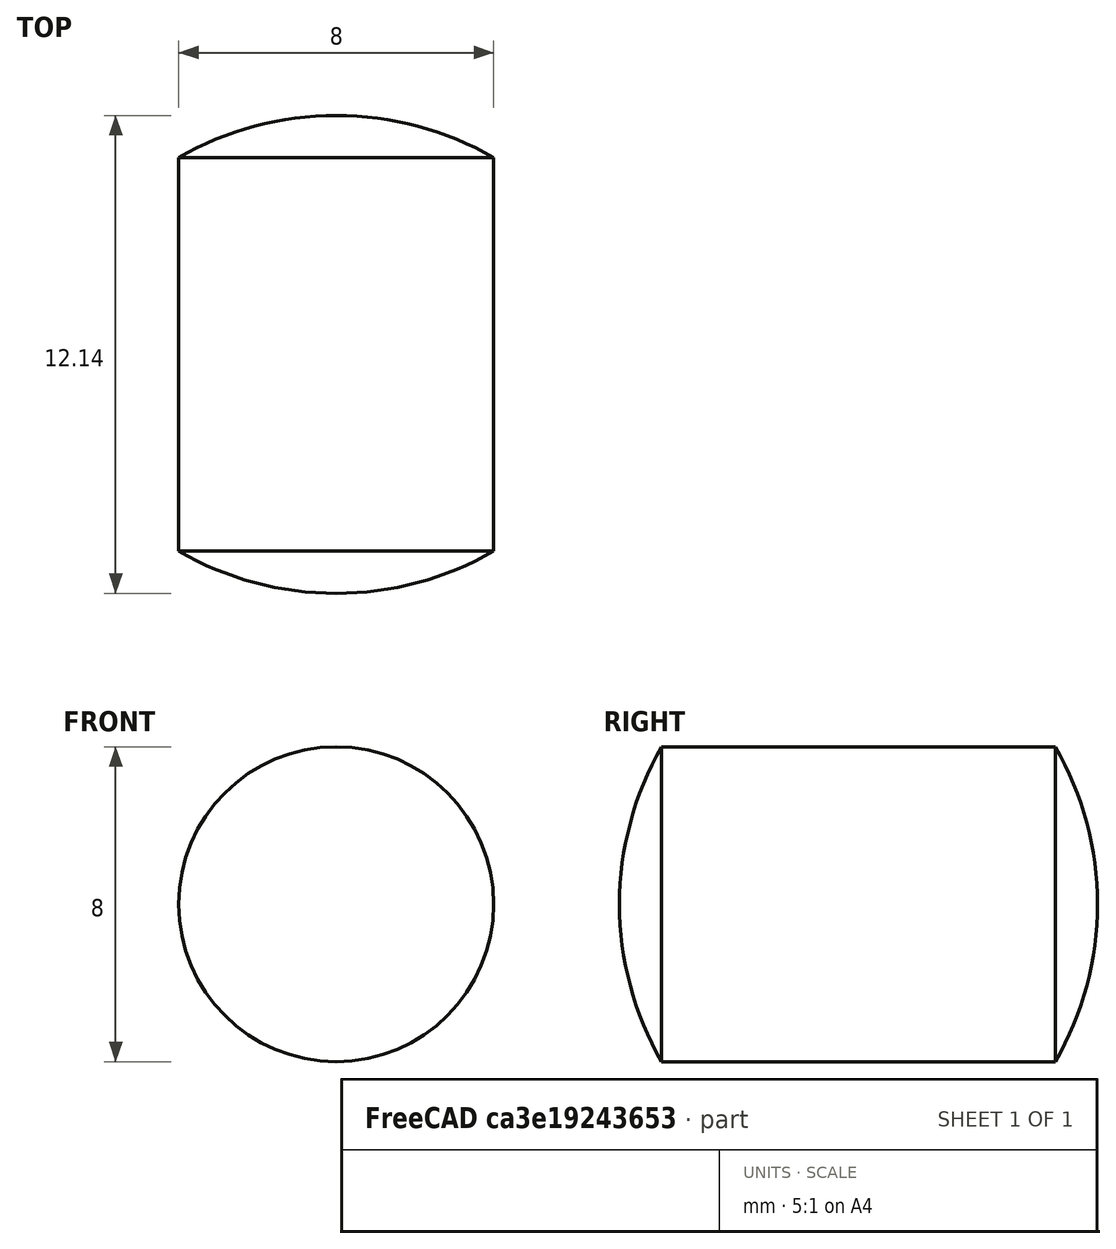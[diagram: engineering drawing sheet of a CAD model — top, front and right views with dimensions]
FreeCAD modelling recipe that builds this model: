
FCSTD DOCUMENT  (FreeCAD 0.15R4470 (Git))
Label: Zyl-Stift_DIN_7-8x10
License: CC-BY 3.0
LicenseURL: http://creativecommons.org/licenses/by/3.0/
objects: Sketcher::SketchObject×1, PartDesign::Revolution×1
note: 3 computed .brp shape members not serialized (recipe doc carries the construction recipe); baked Part::Feature solids carry a one-line shape summary decoded from their .brp

FEATURE [Sketcher::SketchObject] Sketch
  Placement = pos=(0,0,0) rot=(0.57735,0.57735,0.57735;2.0944rad)
  sketch-geometry (4):
    g0: ArcOfCircle CenterX=3.0718 CenterY=0 CenterZ=0 NormalX=0 NormalY=0 NormalZ=1 Radius=8 StartAngle=0 EndAngle=0.523599
    g1: LineSegment StartX=0 StartY=4 StartZ=0 EndX=10 EndY=4 EndZ=0
    g2: LineSegment StartX=-1.0718 StartY=0 StartZ=0 EndX=11.0718 EndY=0 EndZ=0
    g3: ArcOfCircle CenterX=6.9282 CenterY=0 CenterZ=0 NormalX=0 NormalY=0 NormalZ=1 Radius=8 StartAngle=2.61799 EndAngle=3.14159
  constraints (14):
    c: PointOnObject(g2,g-1)
    c: PointOnObject(g1,g-2)
    c: Coincident(g0,g1)
    c: PointOnObject(g0,g-1)
    c: Horizontal(g1)
    c: Coincident(g2,g0)
    c: Horizontal(g2)
    c: Radius(g0) = 8
    c: PointOnObject(g3,g2)
    c: Coincident(g3,g1)
    c: Coincident(g3,g2)
    c: Equal(g3,g0)
    c: DistanceY(g-1,g1) = 4
    c: DistanceX(g1) = 10
FEATURE [PartDesign::Revolution] Revolution  label="Zyl-Stift DIN 7-8x10 #"
  Angle = 360
  Axis = (0,1,0)
  Base = (0,0,0)
  Placement = pos=(0,0,0) rot=(0.57735,0.57735,0.57735;2.0944rad)
  ReferenceAxis = -> Sketch [H_Axis]
  Sketch = -> Sketch
